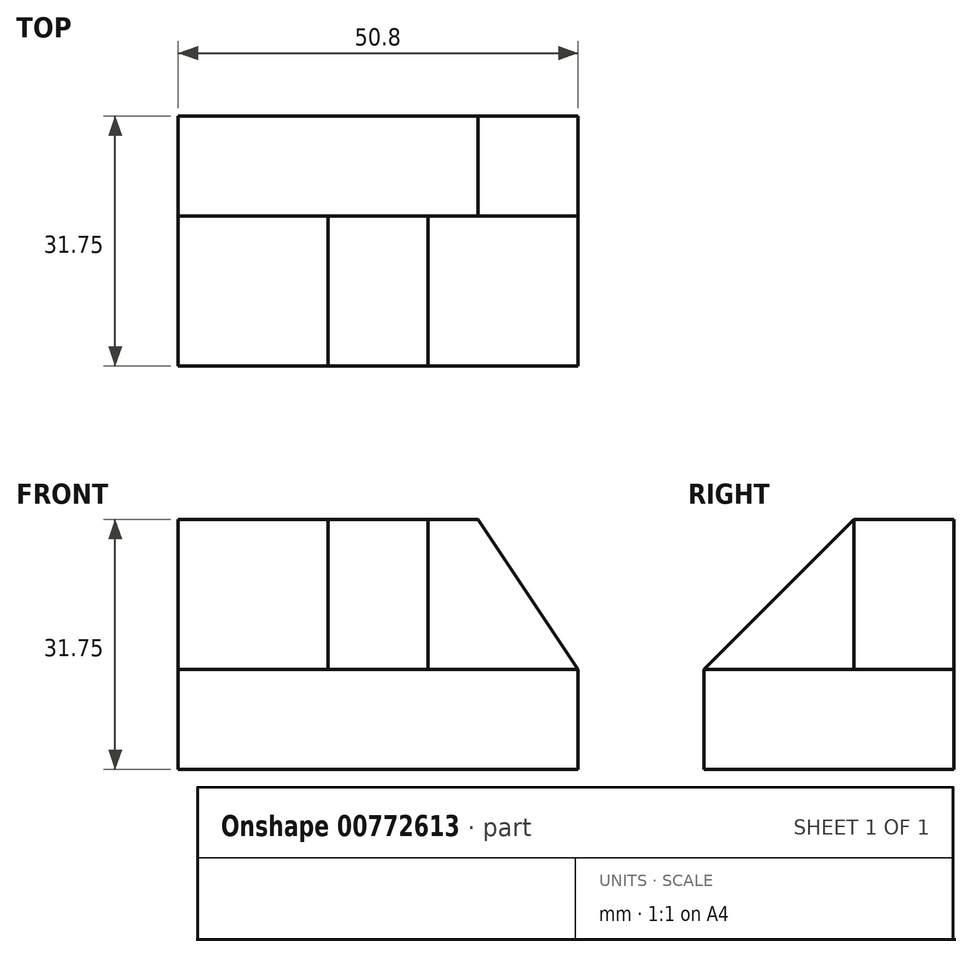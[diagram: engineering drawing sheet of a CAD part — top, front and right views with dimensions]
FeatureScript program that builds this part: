
annotation { "Feature Type Name" : "Feature", "Feature Type Description" : "" }
export const myFeature = defineFeature(function(context is Context, id is Id, definition is map)
    precondition{}
    {
        {
            var Q0;
            Q0=qCreatedBy(makeId("Front.planeOp"),FACE);
            var sketch = newSketch(context, id + "F0", { "sketchPlane" : qUnion([Q0])});
            skLineSegment(sketch, "E0", {"start": v(0, 0) * mm, "end": v(50.8, 0) * mm});
            skLineSegment(sketch, "E1", {"start": v(50.8, 0) * mm, "end": v(50.8, 31.75) * mm});
            skLineSegment(sketch, "E2", {"start": v(50.8, 31.75) * mm, "end": v(0, 31.75) * mm});
            skLineSegment(sketch, "E3", {"start": v(0, 31.75) * mm, "end": v(0, 0) * mm});
            skSolve(sketch);
        }
        {
            var Q0;
            Q0 = qSketchRegion(id + "F0", true);
            extrude(context, id + "F1", {"entities" : qUnion([Q0]), "depth" : 31.75 * mm, "offsetDistance" : 25.4 * mm});
        }
        {
            var Q0;
            Q0=makeQuery(id+"F1.opExtrude","SWEPT_FACE",FACE,{"disambiguationData":[OSD([sQuery(id+"F0.wireOp",EDGE,"E1")])]});
            var sketch = newSketch(context, id + "F2", { "sketchPlane" : qUnion([Q0])});
            skLineSegment(sketch, "E4", {"start": v(-31.75, 0) * mm, "end": v(-31.75, 12.7) * mm});
            skLineSegment(sketch, "E5", {"start": v(0, 31.75) * mm, "end": v(-12.7, 31.75) * mm});
            skLineSegment(sketch, "E6", {"start": v(-12.7, 31.75) * mm, "end": v(-12.7, 12.7) * mm});
            skLineSegment(sketch, "E7", {"start": v(-12.7, 12.7) * mm, "end": v(-31.75, 12.7) * mm});
            skSolve(sketch);
        }
        {
            var Q0;
            Q0 = qSketchRegion(id + "F2", true);
            var Q1;
            {var subQ0=sQuery(id+"F2.wireOp",EDGE,"E6");Q1=makeQuery(id+"F2.imprint","IMPRINT",FACE,{"disambiguationData":[TD([[makeQuery(id+"F2.imprint","IMPRINT",EDGE,{"derivedFrom":subQ0}),-1.0]])]});}
            extrude(context, id + "F3", {"entities" : qUnion([Q0, Q1]), "operationType" : NewBodyOperationType.REMOVE, "oppositeDirection" : true, "depth" : 50.8 * mm, "offsetDistance" : 25.4 * mm});
        }
        {
            var Q0;
            Q0=makeQuery(id+"F1.opExtrude","SWEPT_FACE",FACE,{"disambiguationData":[OSD([sQuery(id+"F0.wireOp",EDGE,"E1")])]});
            var sketch = newSketch(context, id + "F4", { "sketchPlane" : qUnion([Q0])});
            skLineSegment(sketch, "E8", {"start": v(-31.75, 12.7) * mm, "end": v(-12.7, 31.75) * mm});
            skSolve(sketch);
        }
        {
            var Q0;
            Q0=makeQuery(id+"F4.imprint","IMPRINT",FACE,{"disambiguationData":[TD([[makeQuery(id+"F4.imprint","IMPRINT",EDGE,{"derivedFrom":sQuery(id+"F4.wireOp",EDGE,"E8")}),-1.0]])]});
            extrude(context, id + "F5", {"entities" : qUnion([Q0]), "operationType" : NewBodyOperationType.ADD, "depth" : -31.75 * mm, "offsetDistance" : 25.4 * mm});
        }
        {
            var Q0;
            Q0 = qSketchRegion(id + "F4", true);
            var Q1;
            Q1=makeQuery(id+"F4.imprint","IMPRINT",FACE,{"disambiguationData":[TD([[makeQuery(id+"F4.imprint","IMPRINT",EDGE,{"derivedFrom":sQuery(id+"F4.wireOp",EDGE,"E8")}),-1.0]])]});
            extrude(context, id + "F6", {"entities" : qUnion([Q0, Q1]), "operationType" : NewBodyOperationType.REMOVE, "oppositeDirection" : true, "depth" : 19.05 * mm, "offsetDistance" : 25.4 * mm});
        }
        {
            var Q0;
            Q0=makeQuery(id+"F6.boolean.opBoolean","COPY",FACE,{"derivedFrom":makeQuery(id+"F6.opExtrude","SWEPT_FACE",FACE,{"disambiguationData":[OSD([sQuery(id+"F2.wireOp",EDGE,"E6")])]})});
            var sketch = newSketch(context, id + "F7", { "sketchPlane" : qUnion([Q0])});
            skLineSegment(sketch, "E9", {"start": v(50.8, 31.75) * mm, "end": v(38.1, 31.75) * mm});
            skLineSegment(sketch, "E10", {"start": v(50.8, 12.7) * mm, "end": v(38.1, 31.75) * mm});
            skSolve(sketch);
        }
        {
            var Q0;
            Q0=makeQuery(id+"F7.imprint","IMPRINT",FACE,{"disambiguationData":[TD([[makeQuery(id+"F7.imprint","IMPRINT",EDGE,{"derivedFrom":sQuery(id+"F7.wireOp",EDGE,"E9")}),-1.0]])]});
            extrude(context, id + "F8", {"entities" : qUnion([Q0]), "operationType" : NewBodyOperationType.REMOVE, "oppositeDirection" : true, "depth" : 25.4 * mm, "offsetDistance" : 25.4 * mm});
        }
    });
